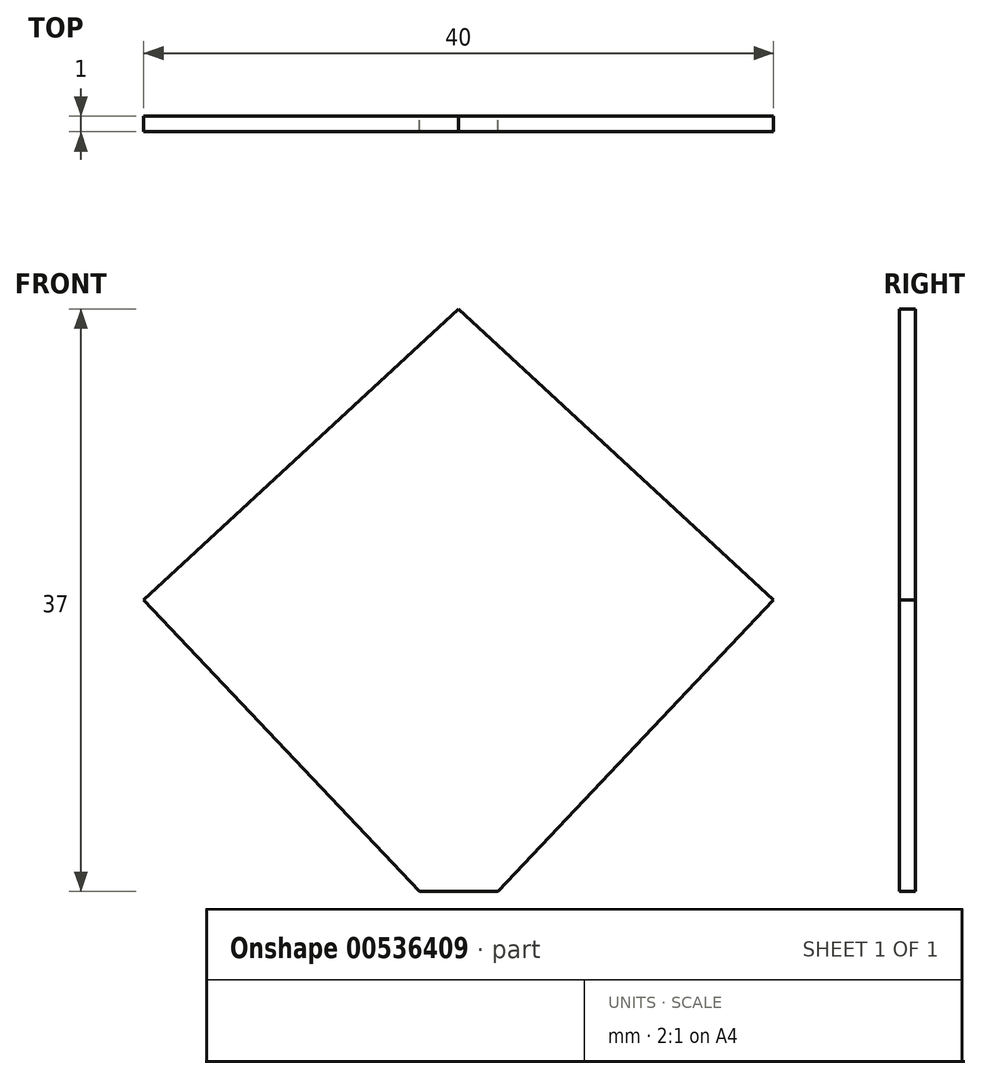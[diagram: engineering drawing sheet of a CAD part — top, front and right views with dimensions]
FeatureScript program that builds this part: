
annotation { "Feature Type Name" : "Feature", "Feature Type Description" : "" }
export const myFeature = defineFeature(function(context is Context, id is Id, definition is map)
    precondition{}
    {
        {
            var Q0;
            Q0=qCreatedBy(makeId("Front.planeOp"),FACE);
            var sketch = newSketch(context, id + "F0", { "sketchPlane" : qUnion([Q0])});
            skLineSegment(sketch, "E0", {"start": v(0, 0) * mm, "end": v(0, 37) * mm});
            skLineSegment(sketch, "E1", {"start": v(0, 0) * mm, "end": v(2.5, 0) * mm});
            skLineSegment(sketch, "E2", {"start": v(0, 0) * mm, "end": v(-2.5, 0) * mm});
            skLineSegment(sketch, "E3", {"start": v(0, 0) * mm, "end": v(0, 18.5) * mm});
            skLineSegment(sketch, "E4", {"start": v(0, 18.5) * mm, "end": v(20, 18.5) * mm});
            skLineSegment(sketch, "E5", {"start": v(0, 18.5) * mm, "end": v(-20, 18.5) * mm});
            skLineSegment(sketch, "E6", {"start": v(0, 37) * mm, "end": v(-20, 18.5) * mm});
            skLineSegment(sketch, "E7", {"start": v(-20, 18.5) * mm, "end": v(-2.5, 0) * mm});
            skLineSegment(sketch, "E8", {"start": v(2.5, 0) * mm, "end": v(20, 18.5) * mm});
            skLineSegment(sketch, "E9", {"start": v(20, 18.5) * mm, "end": v(0, 37) * mm});
            skSolve(sketch);
        }
        {
            var Q0;
            Q0=qSketchRegion(id+"F0",true);
            extrude(context, id + "F1", {"entities" : qUnion([Q0]), "depth" : 1 * mm});
        }
    });
